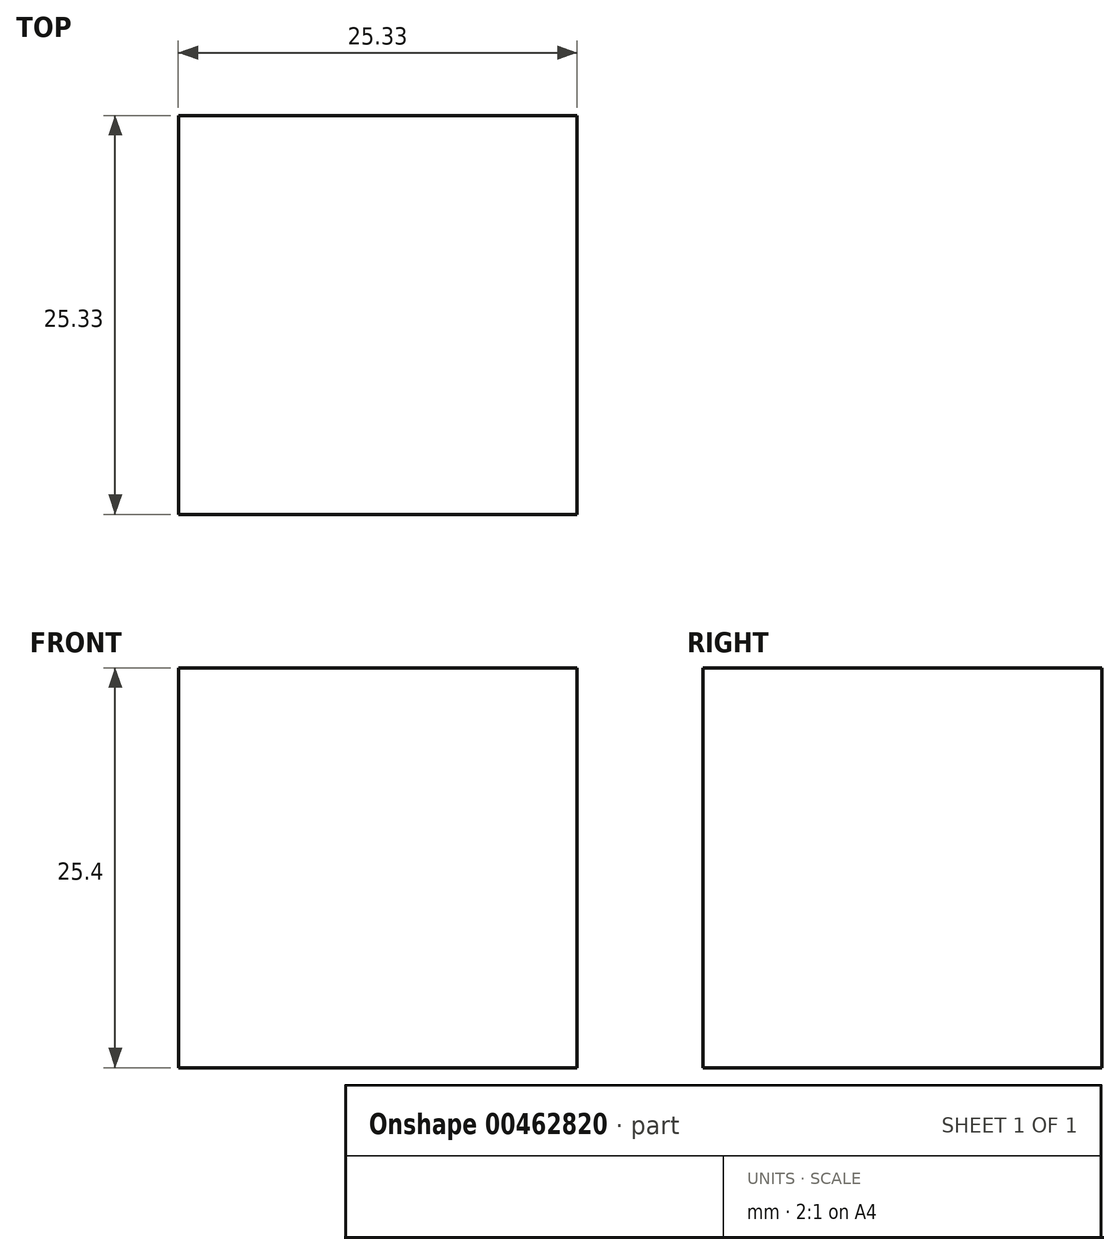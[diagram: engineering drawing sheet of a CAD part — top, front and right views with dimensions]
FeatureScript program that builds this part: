
annotation { "Feature Type Name" : "Feature", "Feature Type Description" : "" }
export const myFeature = defineFeature(function(context is Context, id is Id, definition is map)
    precondition{}
    {
        {
            var Q0;
            Q0=qCreatedBy(makeId("Top.planeOp"),FACE);
            var sketch = newSketch(context, id + "F0", { "sketchPlane" : qUnion([Q0])});
            skLineSegment(sketch, "E0.bottom", {"start": v(-31.95, 25.33) * mm, "end": v(-6.62, 25.33) * mm});
            skLineSegment(sketch, "E0.top", {"start": v(-31.95, 0) * mm, "end": v(-6.62, 0) * mm});
            skLineSegment(sketch, "E0.left", {"start": v(-31.95, 25.33) * mm, "end": v(-31.95, 0) * mm});
            skLineSegment(sketch, "E0.right", {"start": v(-6.62, 25.33) * mm, "end": v(-6.62, 0) * mm});
            skSolve(sketch);
        }
        {
            var Q0;
            Q0 = qSketchRegion(id + "F0", true);
            extrude(context, id + "F1", {"entities" : qUnion([Q0]), "depth" : 25.4 * mm});
        }
    });
